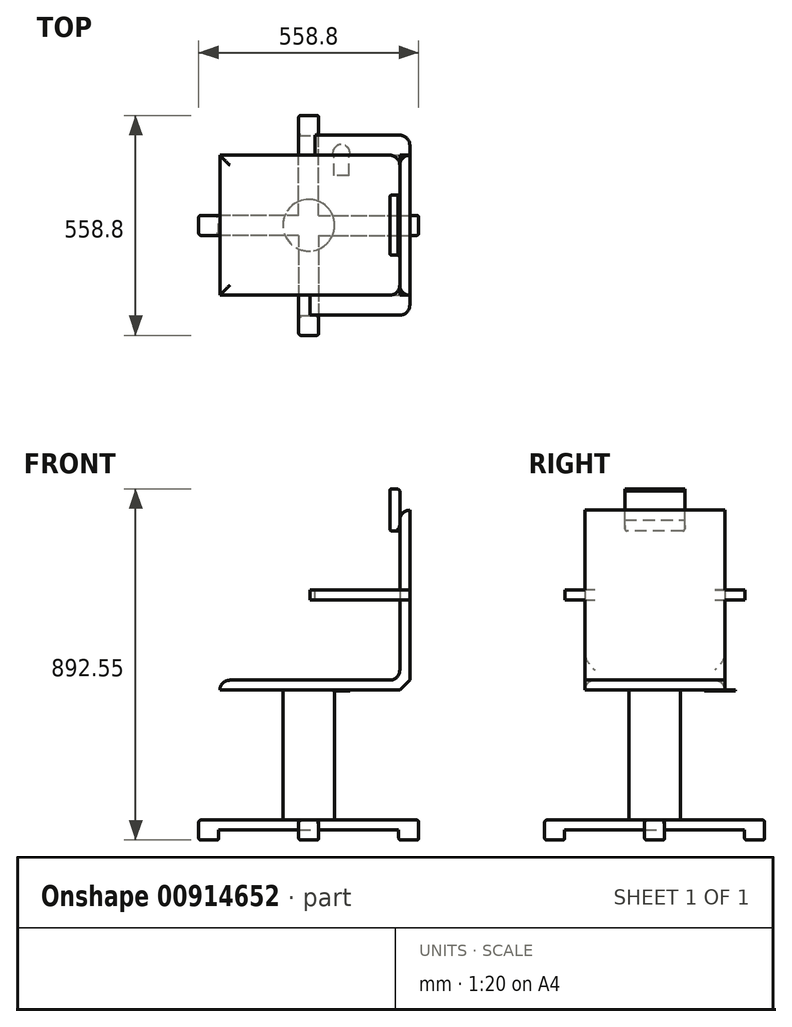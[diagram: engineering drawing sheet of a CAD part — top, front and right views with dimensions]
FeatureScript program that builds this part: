
annotation { "Feature Type Name" : "Feature", "Feature Type Description" : "" }
export const myFeature = defineFeature(function(context is Context, id is Id, definition is map)
    precondition{}
    {
        {
            var Q0;
            Q0=qCreatedBy(makeId("Front.planeOp"),FACE);
            var sketch = newSketch(context, id + "F0", { "sketchPlane" : qUnion([Q0])});
            skLineSegment(sketch, "E0.bottom", {"start": v(-226.04, 372.18) * mm, "end": v(256.56, 372.18) * mm});
            skLineSegment(sketch, "E0.top", {"start": v(-226.04, -85.02) * mm, "end": v(256.56, -85.02) * mm});
            skLineSegment(sketch, "E0.left", {"start": v(-226.04, 372.18) * mm, "end": v(-226.04, -85.02) * mm});
            skLineSegment(sketch, "E0.right", {"start": v(256.56, 372.18) * mm, "end": v(256.56, -85.02) * mm});
            skSolve(sketch);
        }
        {
            var Q0;
            Q0=makeQuery(id+"F0.imprint","IMPRINT",FACE,{"disambiguationData":[TD([[makeQuery(id+"F0.imprint","IMPRINT",EDGE,{"derivedFrom":sQuery(id+"F0.wireOp",EDGE,"E0.bottom")}),-1.0]])]});
            extrude(context, id + "F1", {"entities" : qUnion([Q0]), "depth" : 406.4 * mm, "offsetDistance" : 25.4 * mm});
        }
        {
            var Q0;
            Q0=makeQuery(id+"F1.opExtrude","SWEPT_FACE",FACE,{"disambiguationData":[OSD([sQuery(id+"F0.wireOp",EDGE,"E0.bottom")])]});
            var Q1;
            Q1=makeQuery(id+"F1.opExtrude","SWEPT_FACE",FACE,{"disambiguationData":[OSD([sQuery(id+"F0.wireOp",EDGE,"E0.left")])]});
            shell(context, id + "F2", {"entities" : qUnion([Q0, Q1]), "thickness" : 25.4 * mm});
        }
        {
            var Q0;
            Q0=makeQuery(id+"F1.opExtrude","CAP_FACE",FACE,{"disambiguationData":[OSD([sQuery(id+"F0.wireOp",EDGE,"E0.bottom"),sQuery(id+"F0.wireOp",EDGE,"E0.top"),sQuery(id+"F0.wireOp",EDGE,"E0.left"),sQuery(id+"F0.wireOp",EDGE,"E0.right")])],"isStart":false});
            var sketch = newSketch(context, id + "F3", { "sketchPlane" : qUnion([Q0])});
            skLineSegment(sketch, "E1", {"start": v(256.56, 168.98) * mm, "end": v(-226.04, 168.98) * mm});
            skLineSegment(sketch, "E2", {"start": v(-226.04, 168.98) * mm, "end": v(-226.04, 143.58) * mm});
            skLineSegment(sketch, "E3", {"start": v(-226.04, 143.58) * mm, "end": v(256.56, 143.58) * mm});
            skLineSegment(sketch, "E4.top", {"start": v(256.56, 372.18) * mm, "end": v(-226.04, 372.18) * mm});
            skLineSegment(sketch, "E4.left", {"start": v(256.56, 168.98) * mm, "end": v(256.56, 372.18) * mm});
            skLineSegment(sketch, "E4.right", {"start": v(-226.04, 168.98) * mm, "end": v(-226.04, 372.18) * mm});
            skLineSegment(sketch, "E5.top", {"start": v(-226.04, -85.02) * mm, "end": v(256.56, -85.02) * mm});
            skLineSegment(sketch, "E5.left", {"start": v(-226.04, 143.58) * mm, "end": v(-226.04, -85.02) * mm});
            skLineSegment(sketch, "E5.right", {"start": v(256.56, 143.58) * mm, "end": v(256.56, -85.02) * mm});
            skSolve(sketch);
        }
        {
            var Q0;
            Q0=makeQuery(id+"F3.imprint","IMPRINT",FACE,{"disambiguationData":[TD([[makeQuery(id+"F3.imprint","IMPRINT",EDGE,{"derivedFrom":sQuery(id+"F3.wireOp",EDGE,"E2")}),1.0]])]});
            extrude(context, id + "F4", {"entities" : qUnion([Q0]), "operationType" : NewBodyOperationType.ADD, "depth" : 25.4 * mm, "offsetDistance" : 25.4 * mm});
        }
        {
            var Q0;
            {var subQ0=sQuery(id+"F0.wireOp",EDGE,"E0.right");var subQ1=sQuery(id+"F0.wireOp",EDGE,"E0.left");var subQ2=sQuery(id+"F0.wireOp",EDGE,"E0.bottom");Q0=makeQuery(id+"F4.boolean.opBoolean","SPLIT",FACE,{"disambiguationData":[TD([makeQuery(id+"F1.opExtrude","SWEPT_FACE",FACE,{"disambiguationData":[OSD([subQ2])]})])],"derivedFrom":makeQuery(id+"F1.opExtrude","CAP_FACE",FACE,{"disambiguationData":[OSD([subQ2,sQuery(id+"F0.wireOp",EDGE,"E0.top"),subQ1,subQ0])],"isStart":false})});}
            extrude(context, id + "F5", {"entities" : qUnion([Q0]), "operationType" : NewBodyOperationType.REMOVE, "oppositeDirection" : true, "depth" : 25.4 * mm, "offsetDistance" : 25.4 * mm});
        }
        {
            var Q0;
            {var subQ0=sQuery(id+"F0.wireOp",EDGE,"E0.right");var subQ1=sQuery(id+"F0.wireOp",EDGE,"E0.left");var subQ2=sQuery(id+"F0.wireOp",EDGE,"E0.top");Q0=makeQuery(id+"F4.boolean.opBoolean","SPLIT",FACE,{"disambiguationData":[TD([makeQuery(id+"F1.opExtrude","SWEPT_FACE",FACE,{"disambiguationData":[OSD([subQ2])]})])],"derivedFrom":makeQuery(id+"F1.opExtrude","CAP_FACE",FACE,{"disambiguationData":[OSD([sQuery(id+"F0.wireOp",EDGE,"E0.bottom"),subQ2,subQ1,subQ0])],"isStart":false})});}
            extrude(context, id + "F6", {"entities" : qUnion([Q0]), "operationType" : NewBodyOperationType.REMOVE, "oppositeDirection" : true, "depth" : 25.4 * mm, "offsetDistance" : 25.4 * mm});
        }
        {
            var Q0;
            Q0=makeQuery(id+"F1.opExtrude","CAP_FACE",FACE,{"disambiguationData":[OSD([sQuery(id+"F0.wireOp",EDGE,"E0.bottom"),sQuery(id+"F0.wireOp",EDGE,"E0.top"),sQuery(id+"F0.wireOp",EDGE,"E0.left"),sQuery(id+"F0.wireOp",EDGE,"E0.right")])],"isStart":true});
            var sketch = newSketch(context, id + "F7", { "sketchPlane" : qUnion([Q0])});
            skLineSegment(sketch, "E6", {"start": v(-256.56, 168.98) * mm, "end": v(226.04, 168.98) * mm});
            skLineSegment(sketch, "E7", {"start": v(-256.56, 143.58) * mm, "end": v(226.04, 143.58) * mm});
            skSolve(sketch);
        }
        {
            var Q0;
            Q0 = qSketchRegion(id + "F7", true);
            var Q1;
            {var subQ0=sQuery(id+"F7.wireOp",EDGE,"E6");Q1=makeQuery(id+"F7.imprint","IMPRINT",FACE,{"disambiguationData":[TD([[makeQuery(id+"F7.imprint","IMPRINT",EDGE,{"derivedFrom":subQ0}),-1.0]])]});}
            extrude(context, id + "F8", {"entities" : qUnion([Q0, Q1]), "operationType" : NewBodyOperationType.ADD, "depth" : 25.4 * mm, "offsetDistance" : 25.4 * mm});
        }
        {
            var Q0;
            {var subQ0=sQuery(id+"F0.wireOp",EDGE,"E0.right");var subQ1=sQuery(id+"F0.wireOp",EDGE,"E0.left");var subQ2=sQuery(id+"F0.wireOp",EDGE,"E0.top");Q0=makeQuery(id+"F8.boolean.opBoolean","SPLIT",FACE,{"disambiguationData":[TD([makeQuery(id+"F1.opExtrude","SWEPT_FACE",FACE,{"disambiguationData":[OSD([subQ2])]})])],"derivedFrom":makeQuery(id+"F1.opExtrude","CAP_FACE",FACE,{"disambiguationData":[OSD([sQuery(id+"F0.wireOp",EDGE,"E0.bottom"),subQ2,subQ1,subQ0])],"isStart":true})});}
            extrude(context, id + "F9", {"entities" : qUnion([Q0]), "operationType" : NewBodyOperationType.REMOVE, "oppositeDirection" : true, "depth" : 25.4 * mm, "offsetDistance" : 25.4 * mm});
        }
        {
            var Q0;
            {var subQ0=sQuery(id+"F0.wireOp",EDGE,"E0.right");var subQ1=sQuery(id+"F0.wireOp",EDGE,"E0.left");var subQ2=sQuery(id+"F0.wireOp",EDGE,"E0.bottom");Q0=makeQuery(id+"F8.boolean.opBoolean","SPLIT",FACE,{"disambiguationData":[TD([makeQuery(id+"F1.opExtrude","SWEPT_FACE",FACE,{"disambiguationData":[OSD([subQ2])]})])],"derivedFrom":makeQuery(id+"F1.opExtrude","CAP_FACE",FACE,{"disambiguationData":[OSD([subQ2,sQuery(id+"F0.wireOp",EDGE,"E0.top"),subQ1,subQ0])],"isStart":true})});}
            extrude(context, id + "F10", {"entities" : qUnion([Q0]), "operationType" : NewBodyOperationType.REMOVE, "oppositeDirection" : true, "depth" : 25.4 * mm, "offsetDistance" : 25.4 * mm});
        }
        {
            var Q0;
            {var subQ0=sQuery(id+"F7.wireOp",EDGE,"E6");Q0=makeQuery(id+"F10.boolean.opBoolean","MERGE",FACE,{"derivedFrom":[makeQuery(id+"F8.opExtrude","SWEPT_FACE",FACE,{"disambiguationData":[OSD([subQ0])]})],"fromTools":[makeQuery(id+"F10.opExtrude","SWEPT_FACE",FACE,{"disambiguationData":[OSD([subQ0])]})]});}
            var sketch = newSketch(context, id + "F11", { "sketchPlane" : qUnion([Q0])});
            skLineSegment(sketch, "E8", {"start": v(15.26, 25.4) * mm, "end": v(15.26, -25.4) * mm});
            skSolve(sketch);
        }
        {
            var Q0;
            {var subQ0=sQuery(id+"F3.wireOp",EDGE,"E1");Q0=makeQuery(id+"F5.boolean.opBoolean","MERGE",FACE,{"derivedFrom":[makeQuery(id+"F4.opExtrude","SWEPT_FACE",FACE,{"disambiguationData":[OSD([subQ0])]})],"fromTools":[makeQuery(id+"F5.opExtrude","SWEPT_FACE",FACE,{"disambiguationData":[OSD([subQ0])]})]});}
            var sketch = newSketch(context, id + "F12", { "sketchPlane" : qUnion([Q0])});
            skLineSegment(sketch, "E9", {"start": v(2.56, -381) * mm, "end": v(2.56, -431.8) * mm});
            skSolve(sketch);
        }
        {
            var Q0;
            {var subQ0=sQuery(id+"F12.wireOp",EDGE,"E9");Q0=makeQuery(id+"F12.imprint","IMPRINT",FACE,{"disambiguationData":[TD([[makeQuery(id+"F12.imprint","IMPRINT",EDGE,{"derivedFrom":subQ0}),-1.0]])]});}
            var Q1;
            {var subQ0=sQuery(id+"F11.wireOp",EDGE,"E8");Q1=makeQuery(id+"F11.imprint","IMPRINT",FACE,{"disambiguationData":[TD([[makeQuery(id+"F11.imprint","IMPRINT",EDGE,{"derivedFrom":subQ0}),-1.0]])]});}
            extrude(context, id + "F13", {"entities" : qUnion([Q0, Q1]), "operationType" : NewBodyOperationType.REMOVE, "oppositeDirection" : true, "depth" : 25.4 * mm, "offsetDistance" : 25.4 * mm});
        }
        {
            var Q0;
            Q0=makeQuery(id+"F2.opShell","OFFSET_FACE",FACE,{"disambiguationData":[OSD([sQuery(id+"F0.wireOp",EDGE,"E0.top")])]});
            var Q1;
            {var subQ0=sQuery(id+"F3.wireOp",EDGE,"E4.left");var subQ1=sQuery(id+"F3.wireOp",EDGE,"E1");var subQ2=sQuery(id+"F0.wireOp",EDGE,"E0.right");Q1=makeQuery(id+"F5.boolean.opBoolean","MERGE",EDGE,{"derivedFrom":[makeQuery(id+"F4.opExtrude","SWEPT_EDGE",EDGE,{"disambiguationData":[OSD([subQ2,subQ1,subQ0])]})],"fromTools":[makeQuery(id+"F5.opExtrude","SWEPT_EDGE",EDGE,{"disambiguationData":[OSD([subQ2,subQ1,subQ0])]})]});}
            var Q2;
            Q2=makeQuery(id+"F13.boolean.opBoolean","COPY",EDGE,{"derivedFrom":makeQuery(id+"F13.opExtrude","CAP_EDGE",EDGE,{"disambiguationData":[OSD([sQuery(id+"F12.wireOp",EDGE,"E9")])],"isStart":true})});
            var Q3;
            Q3=makeQuery(id+"F13.boolean.opBoolean","COPY",EDGE,{"derivedFrom":makeQuery(id+"F13.opExtrude","CAP_EDGE",EDGE,{"disambiguationData":[OSD([sQuery(id+"F11.wireOp",EDGE,"E8")])],"isStart":true})});
            var Q4;
            Q4=makeQuery(id+"F13.boolean.opBoolean","COPY",EDGE,{"derivedFrom":makeQuery(id+"F13.opExtrude","CAP_EDGE",EDGE,{"disambiguationData":[OSD([sQuery(id+"F12.wireOp",EDGE,"E9")])],"isStart":false})});
            var Q5;
            Q5=makeQuery(id+"F13.boolean.opBoolean","COPY",EDGE,{"derivedFrom":makeQuery(id+"F13.opExtrude","CAP_EDGE",EDGE,{"disambiguationData":[OSD([sQuery(id+"F11.wireOp",EDGE,"E8")])],"isStart":false})});
            var Q6;
            {var subQ0=sQuery(id+"F7.wireOp",EDGE,"E6");var subQ1=sQuery(id+"F0.wireOp",EDGE,"E0.right");Q6=makeQuery(id+"F10.boolean.opBoolean","MERGE",EDGE,{"derivedFrom":[makeQuery(id+"F8.opExtrude","SWEPT_EDGE",EDGE,{"disambiguationData":[OSD([subQ1,subQ0])]})],"fromTools":[makeQuery(id+"F10.opExtrude","SWEPT_EDGE",EDGE,{"disambiguationData":[OSD([subQ1,subQ0])]})]});}
            var Q7;
            Q7=makeQuery(id+"F8.opExtrude","CAP_EDGE",EDGE,{"disambiguationData":[OSD([sQuery(id+"F0.wireOp",EDGE,"E0.right")])],"isStart":false});
            var Q8;
            Q8=makeQuery(id+"F4.opExtrude","CAP_EDGE",EDGE,{"disambiguationData":[OSD([sQuery(id+"F0.wireOp",EDGE,"E0.right")])],"isStart":false});
            fillet(context, id + "F14", {"entities" : qUnion([Q0, Q1, Q2, Q3, Q4, Q5, Q6, Q7, Q8]), "radius" : 25.4 * mm, "tangentPropagation" : true, "allowEdgeOverflow" : false});
        }
        {
            var Q0;
            Q0=makeQuery(id+"F1.opExtrude","SWEPT_EDGE",EDGE,{"disambiguationData":[OSD([sQuery(id+"F0.wireOp",EDGE,"E0.top"),sQuery(id+"F0.wireOp",EDGE,"E0.right")])]});
            chamfer(context, id + "F15", {"entities" : qUnion([Q0]), "width" : 25.4 * mm, "tangentPropagation" : true});
        }
        {
            var Q0;
            {var subQ0=sQuery(id+"F0.wireOp",EDGE,"E0.right");var subQ2=sQuery(id+"F0.wireOp",EDGE,"E0.left");var subQ3=sQuery(id+"F0.wireOp",EDGE,"E0.top");var subQ4=sQuery(id+"F0.wireOp",EDGE,"E0.bottom");Q0=makeQuery(id+"F10.boolean.opBoolean","SPLIT",EDGE,{"disambiguationData":[topologyDisambiguationEdgeConnected([makeQuery(id+"F10.opExtrude","CAP_FACE",FACE,{"disambiguationData":[OSD([subQ4,subQ3,subQ2,subQ0])],"isStart":false})])],"derivedFrom":makeQuery(id+"F9.boolean.opBoolean","SPLIT",EDGE,{"disambiguationData":[topologyDisambiguationEdgeConnected([makeQuery(id+"F2.opShell","OFFSET_FACE",FACE,{"disambiguationData":[OSD([subQ4,subQ3,subQ2,subQ0]),TDD([makeQuery(id+"F1.opExtrude","CAP_FACE",FACE,{"disambiguationData":[OSD([subQ4,subQ3,subQ2,subQ0])],"isStart":true})])]})])],"derivedFrom":makeQuery(id+"F2.opShell","OFFSET_EDGE",EDGE,{"disambiguationData":[OSD([subQ0]),TDD([makeQuery(id+"F1.opExtrude","CAP_EDGE",EDGE,{"disambiguationData":[OSD([subQ0])],"isStart":true})])]})})});}
            var Q1;
            {var subQ0=sQuery(id+"F0.wireOp",EDGE,"E0.right");Q1=makeQuery(id+"F5.boolean.opBoolean","SPLIT",EDGE,{"disambiguationData":[topologyDisambiguationEdgeConnected([makeQuery(id+"F5.opExtrude","CAP_FACE",FACE,{"disambiguationData":[OSD([sQuery(id+"F0.wireOp",EDGE,"E0.bottom"),sQuery(id+"F0.wireOp",EDGE,"E0.top"),sQuery(id+"F0.wireOp",EDGE,"E0.left"),subQ0])],"isStart":false})])],"derivedFrom":makeQuery(id+"F2.opShell","OFFSET_EDGE",EDGE,{"disambiguationData":[OSD([subQ0]),TDD([makeQuery(id+"F1.opExtrude","CAP_EDGE",EDGE,{"disambiguationData":[OSD([subQ0])],"isStart":false})])]})});}
            var Q2;
            Q2=makeQuery(id+"F2.opShell","OFFSET_EDGE",EDGE,{"disambiguationData":[OSD([sQuery(id+"F0.wireOp",EDGE,"E0.bottom"),sQuery(id+"F0.wireOp",EDGE,"E0.right")])]});
            fillet(context, id + "F16", {"entities" : qUnion([Q0, Q1, Q2]), "radius" : 25.4 * mm, "tangentPropagation" : true, "allowEdgeOverflow" : false});
        }
        {
            var Q0;
            Q0=makeQuery(id+"F1.opExtrude","SWEPT_FACE",FACE,{"disambiguationData":[OSD([sQuery(id+"F0.wireOp",EDGE,"E0.top")])]});
            var sketch = newSketch(context, id + "F17", { "sketchPlane" : qUnion([Q0])});
            skCircle(sketch, "E10", {"center": v(0, 203.2) * mm, "radius": 65.72 * mm});
            skLineSegment(sketch, "E11.bottom", {"start": v(101.77, 76.74) * mm, "end": v(63.59, 76.74) * mm});
            skLineSegment(sketch, "E11.left", {"start": v(101.77, 76.74) * mm, "end": v(101.77, 30.42) * mm});
            skLineSegment(sketch, "E11.right", {"start": v(63.59, 76.74) * mm, "end": v(63.59, 30.42) * mm});
            skArc(sketch, "E12", {"start": v(63.59, 30.42) * mm, "mid": v(82.68, -1.8) * mm, "end": v(101.77, 30.42) * mm});
            skCircle(sketch, "E13", {"center": v(0, 203.2) * mm, "radius": 97.43 * mm});
            skSolve(sketch);
        }
        {
            var Q0;
            {var subQ0=sQuery(id+"F17.wireOp",EDGE,"E12");Q0=makeQuery(id+"F17.imprint","IMPRINT",FACE,{"disambiguationData":[TD([[makeQuery(id+"F17.imprint","IMPRINT",EDGE,{"derivedFrom":subQ0}),1.0]])]});}
            var Q1;
            {var subQ0=sQuery(id+"F17.wireOp",EDGE,"E11.bottom");Q1=makeQuery(id+"F17.imprint","IMPRINT",FACE,{"disambiguationData":[TD([[makeQuery(id+"F17.imprint","IMPRINT",EDGE,{"derivedFrom":subQ0}),1.0]])]});}
            var Q2;
            {var subQ0=sQuery(id+"F17.wireOp",EDGE,"E12");var subQ1=sQuery(id+"F0.wireOp",EDGE,"E0.top");var subQ2=makeQuery(id+"F14.opFillet","BLEND_EDGE",EDGE,{"blendedFrom":[makeQuery(id+"F2.opShell","OFFSET_EDGE",EDGE,{"disambiguationData":[OSD([subQ1]),TDD([makeQuery(id+"F1.opExtrude","CAP_EDGE",EDGE,{"disambiguationData":[OSD([subQ1])],"isStart":true})])]}),makeQuery(id+"F1.opExtrude","SWEPT_FACE",FACE,{"disambiguationData":[OSD([subQ1])]})],"blendedInto":[makeQuery(id+"F1.opExtrude","SWEPT_FACE",FACE,{"disambiguationData":[OSD([subQ1])]})]});var subQ3=makeQuery(id+"F17.imprint","INTERSECT",VERTEX,{"disambiguationData":[OD(0.0)],"derivedFrom":[subQ2,subQ0]});Q2=makeQuery(id+"F17.imprint","IMPRINT",FACE,{"disambiguationData":[TD([[makeQuery(id+"F17.imprint","IMPRINT",EDGE,{"disambiguationData":[TD([[subQ3,-1.0]])],"derivedFrom":subQ0}),1.0]])]});}
            extrude(context, id + "F18", {"entities" : qUnion([Q0, Q1, Q2]), "operationType" : NewBodyOperationType.ADD, "depth" : 2.54 * mm, "offsetDistance" : 25.4 * mm});
        }
        {
            var Q0;
            Q0=makeQuery(id+"F17.imprint","IMPRINT",FACE,{"disambiguationData":[TD([[makeQuery(id+"F17.imprint","IMPRINT",EDGE,{"derivedFrom":sQuery(id+"F17.wireOp",EDGE,"E10")}),1.0]])]});
            extrude(context, id + "F19", {"entities" : qUnion([Q0]), "operationType" : NewBodyOperationType.ADD, "depth" : 330.2 * mm, "offsetDistance" : 25.4 * mm});
        }
        {
            var Q0;
            Q0=makeQuery(id+"F19.opExtrude","CAP_FACE",FACE,{"disambiguationData":[OSD([sQuery(id+"F17.wireOp",EDGE,"E10")])],"isStart":false});
            var sketch = newSketch(context, id + "F20", { "sketchPlane" : qUnion([Q0])});
            skLineSegment(sketch, "E14.bottom", {"start": v(25.4, 228.95) * mm, "end": v(-25.4, 228.95) * mm});
            skLineSegment(sketch, "E14.top", {"start": v(25.4, 482.95) * mm, "end": v(-25.4, 482.95) * mm});
            skLineSegment(sketch, "E14.left", {"start": v(25.4, 228.95) * mm, "end": v(25.4, 482.95) * mm});
            skLineSegment(sketch, "E14.right", {"start": v(-25.4, 228.95) * mm, "end": v(-25.4, 482.95) * mm});
            skLineSegment(sketch, "E15.bottom", {"start": v(25.4, 228.95) * mm, "end": v(279.4, 228.95) * mm});
            skLineSegment(sketch, "E15.top", {"start": v(25.4, 178.15) * mm, "end": v(279.4, 178.15) * mm});
            skLineSegment(sketch, "E15.left", {"start": v(25.4, 228.95) * mm, "end": v(25.4, 178.15) * mm});
            skLineSegment(sketch, "E15.right", {"start": v(279.4, 228.95) * mm, "end": v(279.4, 178.15) * mm});
            skLineSegment(sketch, "E16.bottom", {"start": v(25.4, 178.15) * mm, "end": v(-25.4, 178.15) * mm});
            skLineSegment(sketch, "E16.top", {"start": v(25.4, -75.85) * mm, "end": v(-25.4, -75.85) * mm});
            skLineSegment(sketch, "E16.left", {"start": v(25.4, 178.15) * mm, "end": v(25.4, -75.85) * mm});
            skLineSegment(sketch, "E16.right", {"start": v(-25.4, 178.15) * mm, "end": v(-25.4, -75.85) * mm});
            skLineSegment(sketch, "E17.bottom", {"start": v(-25.4, 178.15) * mm, "end": v(-279.4, 178.15) * mm});
            skLineSegment(sketch, "E17.top", {"start": v(-25.4, 228.95) * mm, "end": v(-279.4, 228.95) * mm});
            skLineSegment(sketch, "E17.left", {"start": v(-25.4, 178.15) * mm, "end": v(-25.4, 228.95) * mm});
            skLineSegment(sketch, "E17.right", {"start": v(-279.4, 178.15) * mm, "end": v(-279.4, 228.95) * mm});
            skSolve(sketch);
        }
        {
            var Q0;
            {var subQ0=sQuery(id+"F20.wireOp",EDGE,"E14.top");Q0=makeQuery(id+"F20.imprint","IMPRINT",FACE,{"disambiguationData":[TD([[makeQuery(id+"F20.imprint","IMPRINT",EDGE,{"derivedFrom":subQ0}),1.0]])]});}
            var Q1;
            {var subQ0=sQuery(id+"F20.wireOp",EDGE,"E17.right");Q1=makeQuery(id+"F20.imprint","IMPRINT",FACE,{"disambiguationData":[TD([[makeQuery(id+"F20.imprint","IMPRINT",EDGE,{"derivedFrom":subQ0}),-1.0]])]});}
            var Q2;
            {var subQ0=sQuery(id+"F20.wireOp",EDGE,"E17.left");Q2=makeQuery(id+"F20.imprint","IMPRINT",FACE,{"disambiguationData":[TD([[makeQuery(id+"F20.imprint","IMPRINT",EDGE,{"derivedFrom":subQ0}),1.0]])]});}
            var Q3;
            Q3=makeQuery(id+"F20.imprint","IMPRINT",FACE,{"disambiguationData":[TD([[makeQuery(id+"F20.imprint","IMPRINT",EDGE,{"derivedFrom":sQuery(id+"F20.wireOp",EDGE,"E14.bottom")}),1.0]])]});
            var Q4;
            {var subQ0=sQuery(id+"F20.wireOp",EDGE,"E14.bottom");Q4=makeQuery(id+"F20.imprint","IMPRINT",FACE,{"disambiguationData":[TD([[makeQuery(id+"F20.imprint","IMPRINT",EDGE,{"derivedFrom":subQ0}),-1.0]])]});}
            var Q5;
            {var subQ0=sQuery(id+"F20.wireOp",EDGE,"E16.bottom");Q5=makeQuery(id+"F20.imprint","IMPRINT",FACE,{"disambiguationData":[TD([[makeQuery(id+"F20.imprint","IMPRINT",EDGE,{"derivedFrom":subQ0}),1.0]])]});}
            var Q6;
            {var subQ0=sQuery(id+"F20.wireOp",EDGE,"E15.left");Q6=makeQuery(id+"F20.imprint","IMPRINT",FACE,{"disambiguationData":[TD([[makeQuery(id+"F20.imprint","IMPRINT",EDGE,{"derivedFrom":subQ0}),1.0]])]});}
            var Q7;
            {var subQ0=sQuery(id+"F20.wireOp",EDGE,"E15.right");Q7=makeQuery(id+"F20.imprint","IMPRINT",FACE,{"disambiguationData":[TD([[makeQuery(id+"F20.imprint","IMPRINT",EDGE,{"derivedFrom":subQ0}),-1.0]])]});}
            var Q8;
            {var subQ0=sQuery(id+"F20.wireOp",EDGE,"E16.top");Q8=makeQuery(id+"F20.imprint","IMPRINT",FACE,{"disambiguationData":[TD([[makeQuery(id+"F20.imprint","IMPRINT",EDGE,{"derivedFrom":subQ0}),-1.0]])]});}
            extrude(context, id + "F21", {"entities" : qUnion([Q0, Q1, Q2, Q3, Q4, Q5, Q6, Q7, Q8]), "operationType" : NewBodyOperationType.ADD, "depth" : 25.4 * mm, "offsetDistance" : 25.4 * mm});
        }
        {
            var Q0;
            Q0=makeQuery(id+"F21.opExtrude","CAP_FACE",FACE,{"disambiguationData":[OSD([sQuery(id+"F20.wireOp",EDGE,"E14.top"),sQuery(id+"F20.wireOp",EDGE,"E14.left"),sQuery(id+"F20.wireOp",EDGE,"E14.right"),sQuery(id+"F20.wireOp",EDGE,"E15.bottom"),sQuery(id+"F20.wireOp",EDGE,"E15.top"),sQuery(id+"F20.wireOp",EDGE,"E15.right"),sQuery(id+"F20.wireOp",EDGE,"E16.top"),sQuery(id+"F20.wireOp",EDGE,"E16.left"),sQuery(id+"F20.wireOp",EDGE,"E16.right"),sQuery(id+"F20.wireOp",EDGE,"E17.bottom"),sQuery(id+"F20.wireOp",EDGE,"E17.top"),sQuery(id+"F20.wireOp",EDGE,"E17.right")])],"isStart":false});
            var sketch = newSketch(context, id + "F22", { "sketchPlane" : qUnion([Q0])});
            skPoint(sketch, "E18.centerSnap0", {"position": v(0, -75.85) * mm});
            skPoint(sketch, "E19.centerSnap0", {"position": v(-279.4, 203.55) * mm});
            skLineSegment(sketch, "E20.bottom", {"start": v(-279.4, 228.95) * mm, "end": v(-228.6, 228.95) * mm});
            skLineSegment(sketch, "E20.top", {"start": v(-279.4, 178.15) * mm, "end": v(-228.6, 178.15) * mm});
            skLineSegment(sketch, "E20.left", {"start": v(-279.4, 228.95) * mm, "end": v(-279.4, 178.15) * mm});
            skLineSegment(sketch, "E20.right", {"start": v(-228.6, 228.95) * mm, "end": v(-228.6, 178.15) * mm});
            skLineSegment(sketch, "E21.bottom", {"start": v(-25.4, 482.95) * mm, "end": v(25.4, 482.95) * mm});
            skLineSegment(sketch, "E21.top", {"start": v(-25.4, 432.15) * mm, "end": v(25.4, 432.15) * mm});
            skLineSegment(sketch, "E21.left", {"start": v(-25.4, 482.95) * mm, "end": v(-25.4, 432.15) * mm});
            skLineSegment(sketch, "E21.right", {"start": v(25.4, 482.95) * mm, "end": v(25.4, 432.15) * mm});
            skLineSegment(sketch, "E22.bottom", {"start": v(279.4, 228.95) * mm, "end": v(228.6, 228.95) * mm});
            skLineSegment(sketch, "E22.top", {"start": v(279.4, 178.15) * mm, "end": v(228.6, 178.15) * mm});
            skLineSegment(sketch, "E22.left", {"start": v(279.4, 228.95) * mm, "end": v(279.4, 178.15) * mm});
            skLineSegment(sketch, "E22.right", {"start": v(228.6, 228.95) * mm, "end": v(228.6, 178.15) * mm});
            skLineSegment(sketch, "E23.bottom", {"start": v(-25.4, -75.85) * mm, "end": v(25.4, -75.85) * mm});
            skLineSegment(sketch, "E23.top", {"start": v(-25.4, -25.05) * mm, "end": v(25.4, -25.05) * mm});
            skLineSegment(sketch, "E23.left", {"start": v(-25.4, -75.85) * mm, "end": v(-25.4, -25.05) * mm});
            skLineSegment(sketch, "E23.right", {"start": v(25.4, -75.85) * mm, "end": v(25.4, -25.05) * mm});
            skSolve(sketch);
        }
        {
            var Q0;
            Q0=makeQuery(id+"F22.imprint","IMPRINT",FACE,{"disambiguationData":[TD([[makeQuery(id+"F22.imprint","IMPRINT",EDGE,{"derivedFrom":sQuery(id+"F22.wireOp",EDGE,"E20.bottom")}),1.0]])]});
            var Q1;
            Q1=makeQuery(id+"F22.imprint","IMPRINT",FACE,{"disambiguationData":[TD([[makeQuery(id+"F22.imprint","IMPRINT",EDGE,{"derivedFrom":sQuery(id+"F22.wireOp",EDGE,"E21.bottom")}),1.0]])]});
            var Q2;
            Q2=makeQuery(id+"F22.imprint","IMPRINT",FACE,{"disambiguationData":[TD([[makeQuery(id+"F22.imprint","IMPRINT",EDGE,{"derivedFrom":sQuery(id+"F22.wireOp",EDGE,"E22.bottom")}),-1.0]])]});
            var Q3;
            Q3=makeQuery(id+"F22.imprint","IMPRINT",FACE,{"disambiguationData":[TD([[makeQuery(id+"F22.imprint","IMPRINT",EDGE,{"derivedFrom":sQuery(id+"F22.wireOp",EDGE,"E23.bottom")}),-1.0]])]});
            extrude(context, id + "F23", {"entities" : qUnion([Q0, Q1, Q2, Q3]), "operationType" : NewBodyOperationType.ADD, "depth" : 25.4 * mm, "offsetDistance" : 25.4 * mm});
        }
        {
            var Q0;
            Q0=makeQuery(id+"F23.opExtrude","CAP_EDGE",EDGE,{"disambiguationData":[OSD([sQuery(id+"F22.wireOp",EDGE,"E20.left")])],"isStart":false});
            var Q1;
            Q1=makeQuery(id+"F23.opExtrude","CAP_EDGE",EDGE,{"disambiguationData":[OSD([sQuery(id+"F22.wireOp",EDGE,"E20.bottom")])],"isStart":false});
            var Q2;
            Q2=makeQuery(id+"F23.opExtrude","CAP_EDGE",EDGE,{"disambiguationData":[OSD([sQuery(id+"F22.wireOp",EDGE,"E20.right")])],"isStart":false});
            var Q3;
            Q3=makeQuery(id+"F23.opExtrude","CAP_FACE",FACE,{"disambiguationData":[OSD([sQuery(id+"F22.wireOp",EDGE,"E20.bottom"),sQuery(id+"F22.wireOp",EDGE,"E20.top"),sQuery(id+"F22.wireOp",EDGE,"E20.left"),sQuery(id+"F22.wireOp",EDGE,"E20.right")])],"isStart":false});
            var Q4;
            Q4=makeQuery(id+"F23.opExtrude","CAP_FACE",FACE,{"disambiguationData":[OSD([sQuery(id+"F22.wireOp",EDGE,"E21.bottom"),sQuery(id+"F22.wireOp",EDGE,"E21.top"),sQuery(id+"F22.wireOp",EDGE,"E21.left"),sQuery(id+"F22.wireOp",EDGE,"E21.right")])],"isStart":false});
            var Q5;
            Q5=makeQuery(id+"F23.opExtrude","CAP_FACE",FACE,{"disambiguationData":[OSD([sQuery(id+"F22.wireOp",EDGE,"E22.bottom"),sQuery(id+"F22.wireOp",EDGE,"E22.top"),sQuery(id+"F22.wireOp",EDGE,"E22.left"),sQuery(id+"F22.wireOp",EDGE,"E22.right")])],"isStart":false});
            var Q6;
            Q6=makeQuery(id+"F23.opExtrude","CAP_FACE",FACE,{"disambiguationData":[OSD([sQuery(id+"F22.wireOp",EDGE,"E23.bottom"),sQuery(id+"F22.wireOp",EDGE,"E23.top"),sQuery(id+"F22.wireOp",EDGE,"E23.left"),sQuery(id+"F22.wireOp",EDGE,"E23.right")])],"isStart":false});
            fillet(context, id + "F24", {"entities" : qUnion([Q0, Q1, Q2, Q3, Q4, Q5, Q6]), "radius" : 5.08 * mm, "tangentPropagation" : true, "allowEdgeOverflow" : false});
        }
        {
            var Q0;
            Q0=makeQuery(id+"F23.boolean.opBoolean","MERGE",EDGE,{"derivedFrom":[makeQuery(id+"F21.opExtrude","SWEPT_EDGE",EDGE,{"disambiguationData":[OSD([sQuery(id+"F20.wireOp",EDGE,"E17.bottom"),sQuery(id+"F20.wireOp",EDGE,"E17.right")])]}),makeQuery(id+"F23.opExtrude","SWEPT_EDGE",EDGE,{"disambiguationData":[OSD([sQuery(id+"F22.wireOp",EDGE,"E20.top"),sQuery(id+"F22.wireOp",EDGE,"E20.left")])]})]});
            var Q1;
            Q1=makeQuery(id+"F23.boolean.opBoolean","MERGE",FACE,{"derivedFrom":[makeQuery(id+"F21.opExtrude","SWEPT_FACE",FACE,{"disambiguationData":[OSD([sQuery(id+"F20.wireOp",EDGE,"E17.right")])]}),makeQuery(id+"F23.opExtrude","SWEPT_FACE",FACE,{"disambiguationData":[OSD([sQuery(id+"F22.wireOp",EDGE,"E20.left")])]})]});
            var Q2;
            Q2=makeQuery(id+"F23.boolean.opBoolean","MERGE",FACE,{"derivedFrom":[makeQuery(id+"F21.opExtrude","SWEPT_FACE",FACE,{"disambiguationData":[OSD([sQuery(id+"F20.wireOp",EDGE,"E14.top")])]}),makeQuery(id+"F23.opExtrude","SWEPT_FACE",FACE,{"disambiguationData":[OSD([sQuery(id+"F22.wireOp",EDGE,"E21.bottom")])]})]});
            var Q3;
            Q3=makeQuery(id+"F23.boolean.opBoolean","MERGE",FACE,{"derivedFrom":[makeQuery(id+"F21.opExtrude","SWEPT_FACE",FACE,{"disambiguationData":[OSD([sQuery(id+"F20.wireOp",EDGE,"E15.right")])]}),makeQuery(id+"F23.opExtrude","SWEPT_FACE",FACE,{"disambiguationData":[OSD([sQuery(id+"F22.wireOp",EDGE,"E22.left")])]})]});
            var Q4;
            Q4=makeQuery(id+"F23.boolean.opBoolean","MERGE",FACE,{"derivedFrom":[makeQuery(id+"F21.opExtrude","SWEPT_FACE",FACE,{"disambiguationData":[OSD([sQuery(id+"F20.wireOp",EDGE,"E16.top")])]}),makeQuery(id+"F23.opExtrude","SWEPT_FACE",FACE,{"disambiguationData":[OSD([sQuery(id+"F22.wireOp",EDGE,"E23.bottom")])]})]});
            fillet(context, id + "F25", {"entities" : qUnion([Q0, Q1, Q2, Q3, Q4]), "radius" : 5.08 * mm, "tangentPropagation" : true, "allowEdgeOverflow" : false});
        }
        {
            var Q0;
            Q0=makeQuery(id+"F2.opShell","OFFSET_FACE",FACE,{"disambiguationData":[OSD([sQuery(id+"F0.wireOp",EDGE,"E0.right")])]});
            var sketch = newSketch(context, id + "F26", { "sketchPlane" : qUnion([Q0])});
            skLineSegment(sketch, "E24.bottom", {"start": v(127, 319.7) * mm, "end": v(279.4, 319.7) * mm});
            skLineSegment(sketch, "E24.top", {"start": v(127, 426.53) * mm, "end": v(279.4, 426.53) * mm});
            skLineSegment(sketch, "E24.left", {"start": v(127, 319.7) * mm, "end": v(127, 426.53) * mm});
            skLineSegment(sketch, "E24.right", {"start": v(279.4, 319.7) * mm, "end": v(279.4, 426.53) * mm});
            skSolve(sketch);
        }
        {
            var Q0;
            {var subQ0=sQuery(id+"F26.wireOp",EDGE,"E24.top");Q0=makeQuery(id+"F26.imprint","IMPRINT",FACE,{"disambiguationData":[TD([[makeQuery(id+"F26.imprint","IMPRINT",EDGE,{"derivedFrom":subQ0}),-1.0]])]});}
            var Q1;
            {var subQ0=sQuery(id+"F26.wireOp",EDGE,"E24.bottom");Q1=makeQuery(id+"F26.imprint","IMPRINT",FACE,{"disambiguationData":[TD([[makeQuery(id+"F26.imprint","IMPRINT",EDGE,{"derivedFrom":subQ0}),1.0]])]});}
            extrude(context, id + "F27", {"entities" : qUnion([Q0, Q1]), "operationType" : NewBodyOperationType.ADD, "depth" : 25.4 * mm, "offsetDistance" : 25.4 * mm});
        }
        {
            var Q0;
            Q0=makeQuery(id+"F27.opExtrude","CAP_FACE",FACE,{"disambiguationData":[OSD([sQuery(id+"F26.wireOp",EDGE,"E24.bottom"),sQuery(id+"F26.wireOp",EDGE,"E24.top"),sQuery(id+"F26.wireOp",EDGE,"E24.left"),sQuery(id+"F26.wireOp",EDGE,"E24.right")])],"isStart":false});
            var Q1;
            Q1=makeQuery(id+"F27.opExtrude","SWEPT_FACE",FACE,{"disambiguationData":[OSD([sQuery(id+"F26.wireOp",EDGE,"E24.bottom")])]});
            fillet(context, id + "F28", {"entities" : qUnion([Q0, Q1]), "radius" : 5.08 * mm, "tangentPropagation" : true, "allowEdgeOverflow" : false});
        }
        {
            var Q0;
            Q0=makeQuery(id+"F27.opExtrude","CAP_EDGE",EDGE,{"disambiguationData":[OSD([sQuery(id+"F26.wireOp",EDGE,"E24.top")])],"isStart":true});
            chamfer(context, id + "F29", {"entities" : qUnion([Q0]), "width" : 5.08 * mm, "tangentPropagation" : true});
        }
    });
